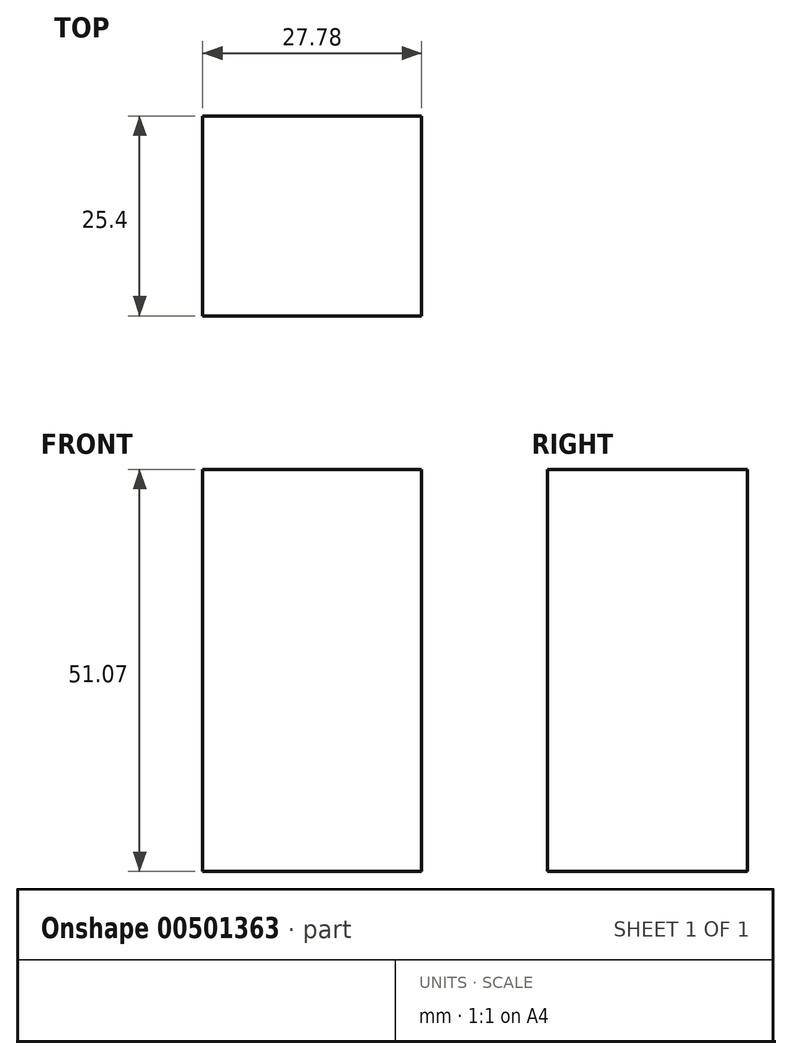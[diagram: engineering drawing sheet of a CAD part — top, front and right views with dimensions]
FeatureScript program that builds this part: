
annotation { "Feature Type Name" : "Feature", "Feature Type Description" : "" }
export const myFeature = defineFeature(function(context is Context, id is Id, definition is map)
    precondition{}
    {
        {
            var Q0;
            Q0=qCreatedBy(makeId("Front.planeOp"),FACE);
            var sketch = newSketch(context, id + "F0", { "sketchPlane" : qUnion([Q0])});
            skLineSegment(sketch, "E0.bottom", {"start": v(-56.97, 33.15) * mm, "end": v(-29.2, 33.15) * mm});
            skLineSegment(sketch, "E0.top", {"start": v(-56.97, -17.92) * mm, "end": v(-29.2, -17.92) * mm});
            skLineSegment(sketch, "E0.left", {"start": v(-56.97, 33.15) * mm, "end": v(-56.97, -17.92) * mm});
            skLineSegment(sketch, "E0.right", {"start": v(-29.2, 33.15) * mm, "end": v(-29.2, -17.92) * mm});
            skSolve(sketch);
        }
        {
            var Q0;
            Q0=makeQuery(id+"F0.imprint","IMPRINT",FACE,{"disambiguationData":[TD([[makeQuery(id+"F0.imprint","IMPRINT",EDGE,{"derivedFrom":sQuery(id+"F0.wireOp",EDGE,"E0.bottom")}),-1.0]])]});
            extrude(context, id + "F1", {"entities" : qUnion([Q0]), "depth" : 25.4 * mm});
        }
    });
